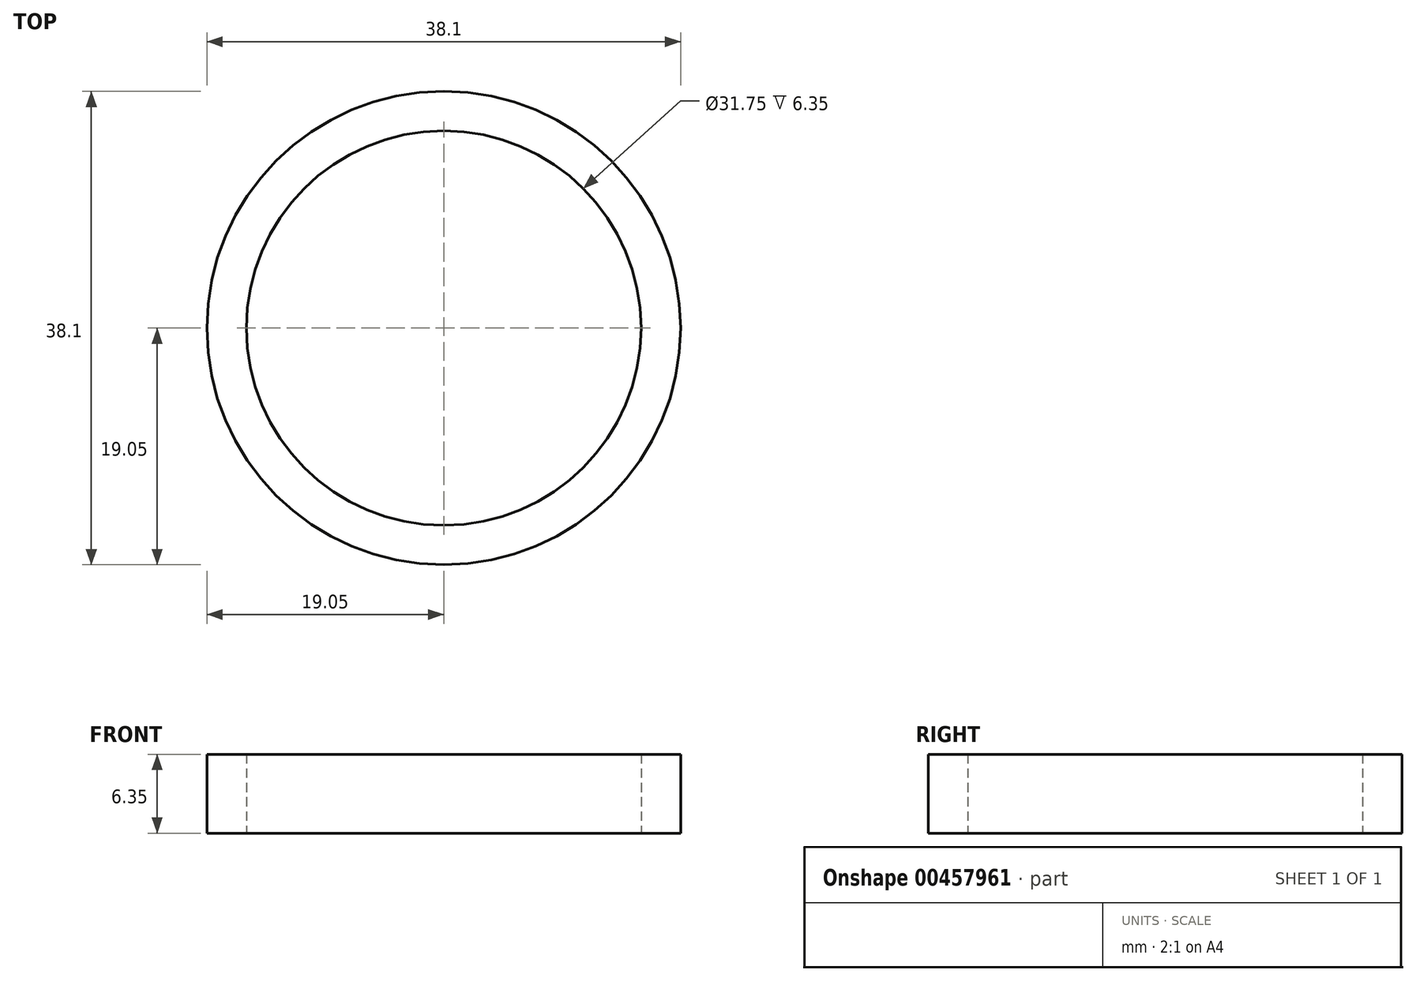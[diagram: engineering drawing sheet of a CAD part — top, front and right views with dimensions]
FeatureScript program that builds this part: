
annotation { "Feature Type Name" : "Feature", "Feature Type Description" : "" }
export const myFeature = defineFeature(function(context is Context, id is Id, definition is map)
    precondition{}
    {
        {
            var Q0;
            Q0=qCreatedBy(makeId("Front.planeOp"),FACE);
            var sketch = newSketch(context, id + "F0", { "sketchPlane" : qUnion([Q0])});
            skLineSegment(sketch, "E0", {"start": v(0, 0) * mm, "end": v(0, 29.1) * mm, "construction": true});
            skLineSegment(sketch, "E1", {"start": v(-15.88, 0) * mm, "end": v(-19.05, 0) * mm});
            skLineSegment(sketch, "E2", {"start": v(-19.05, 0) * mm, "end": v(-19.05, 6.35) * mm});
            skLineSegment(sketch, "E3", {"start": v(-19.05, 6.35) * mm, "end": v(-15.88, 6.35) * mm});
            skLineSegment(sketch, "E4", {"start": v(-15.88, 6.35) * mm, "end": v(-15.88, 0) * mm});
            skSolve(sketch);
        }
        {
            var Q0;
            Q0=qSketchRegion(id+"F0",true);
            var Q1;
            Q1=sQuery(id+"F0.wireOp",EDGE,"E0");
            revolve(context, id + "F1", {"entities" : qUnion([Q0]), "axis" : qUnion([Q1]), "revolveType" : RevolveType.FULL});
        }
    });
